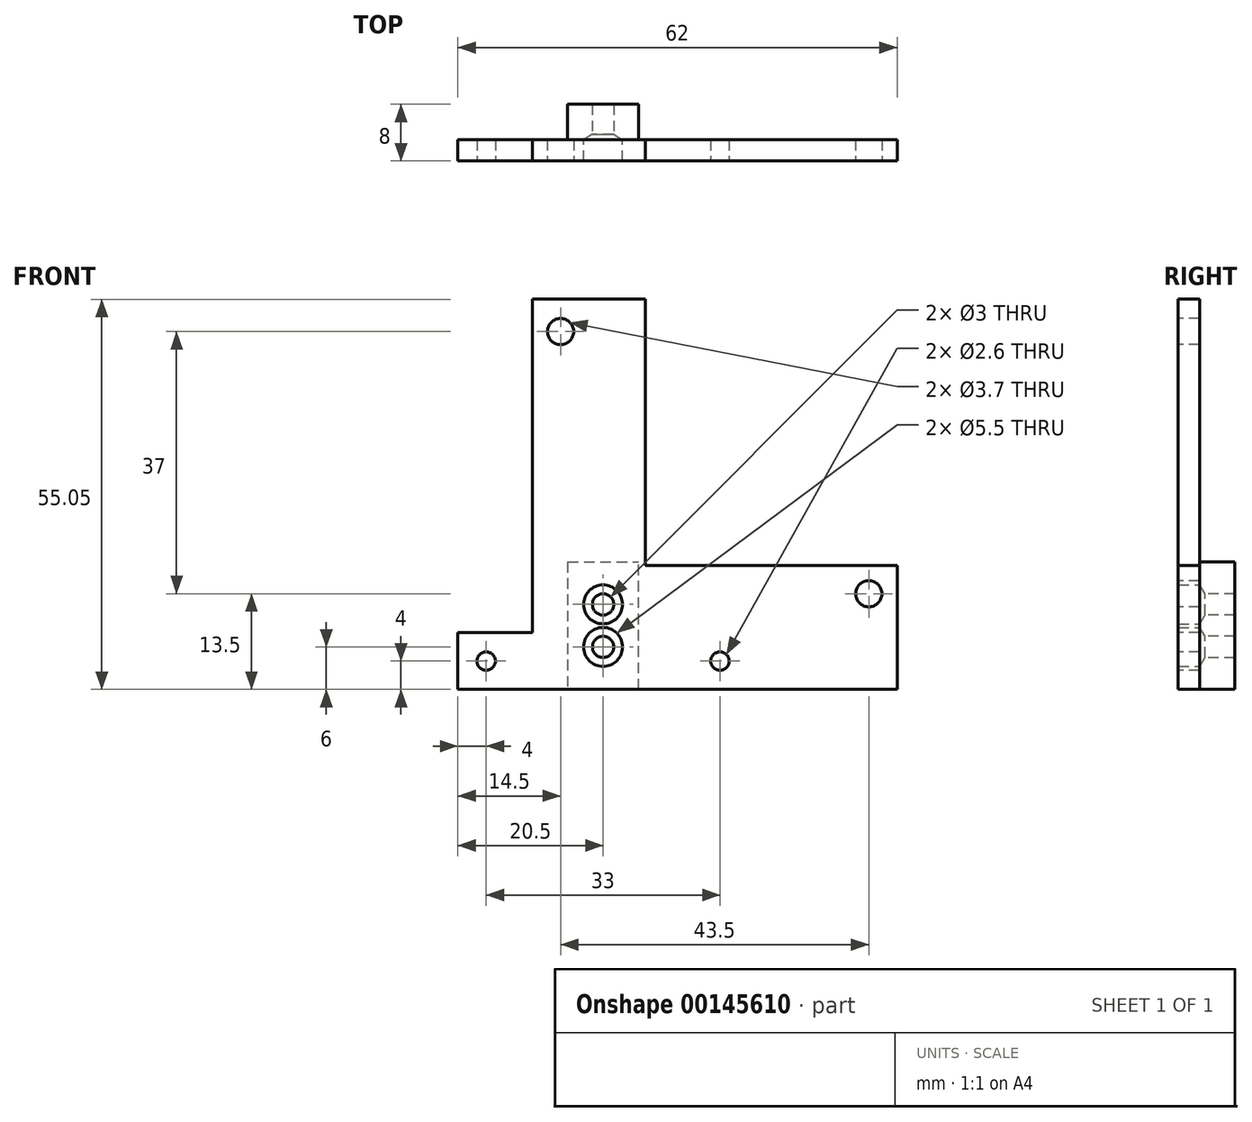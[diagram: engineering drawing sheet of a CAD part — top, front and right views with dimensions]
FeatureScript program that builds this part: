
annotation { "Feature Type Name" : "Feature", "Feature Type Description" : "" }
export const myFeature = defineFeature(function(context is Context, id is Id, definition is map)
    precondition{}
    {
        {
            var Q0;
            Q0=qCreatedBy(makeId("Front.planeOp"),FACE);
            var sketch = newSketch(context, id + "F0", { "sketchPlane" : qUnion([Q0])});
            skLineSegment(sketch, "E0", {"start": v(10, 73.44) * mm, "end": v(10, -53.24) * mm, "construction": true});
            skCircle(sketch, "E1", {"center": v(-6.5, -1) * mm, "radius": 1.3 * mm});
            skCircle(sketch, "E2", {"center": v(26.5, -1) * mm, "radius": 1.3 * mm});
            skCircle(sketch, "E3", {"center": v(4, 45.5) * mm, "radius": 1.85 * mm});
            skCircle(sketch, "E4", {"center": v(47.5, 8.5) * mm, "radius": 1.85 * mm});
            skLineSegment(sketch, "E5", {"start": v(-10.5, 3) * mm, "end": v(-10.5, -5) * mm});
            skLineSegment(sketch, "E6", {"start": v(-10.5, -5) * mm, "end": v(51.5, -5) * mm});
            skLineSegment(sketch, "E7", {"start": v(51.5, -5) * mm, "end": v(51.5, 12.5) * mm});
            skLineSegment(sketch, "E8", {"start": v(51.5, 12.5) * mm, "end": v(16, 12.5) * mm});
            skLineSegment(sketch, "E9", {"start": v(16, 12.5) * mm, "end": v(16, 50.05) * mm});
            skLineSegment(sketch, "E10", {"start": v(16, 50.05) * mm, "end": v(0, 50.05) * mm});
            skLineSegment(sketch, "E11", {"start": v(0, 50.05) * mm, "end": v(0, 3) * mm});
            skLineSegment(sketch, "E12", {"start": v(0, 3) * mm, "end": v(-10.5, 3) * mm});
            skCircle(sketch, "E13", {"center": v(10, 7) * mm, "radius": 1.5 * mm});
            skCircle(sketch, "E14", {"center": v(10, 1) * mm, "radius": 1.5 * mm});
            skLineSegment(sketch, "E15.right", {"start": v(15, -5) * mm, "end": v(15, 13) * mm});
            skLineSegment(sketch, "E16", {"start": v(5, 13) * mm, "end": v(5, -5) * mm});
            skLineSegment(sketch, "E17", {"start": v(5, 13) * mm, "end": v(15, 13) * mm});
            skSolve(sketch);
        }
        {
            var Q0;
            Q0=qSketchRegion(id+"F0",true);
            extrude(context, id + "F1", {"entities" : qUnion([Q0]), "oppositeDirection" : true, "depth" : 3 * mm, "offsetDistance" : 25 * mm});
        }
        {
            var Q0;
            Q0=makeQuery(id+"F0.imprint","IMPRINT",FACE,{"disambiguationData":[TD([[makeQuery(id+"F0.imprint","IMPRINT",EDGE,{"derivedFrom":sQuery(id+"F0.wireOp",EDGE,"E13")}),-1.0]])]});
            extrude(context, id + "F2", {"entities" : qUnion([Q0]), "operationType" : NewBodyOperationType.ADD, "oppositeDirection" : true, "depth" : 8 * mm, "offsetDistance" : 25 * mm});
        }
        {
            var Q0;
            Q0=sQuery(id+"F0.wireOp",VERTEX,"E13.center");
            var Q1;
            Q1=sQuery(id+"F0.wireOp",VERTEX,"E14.center");
            var Q2;
            Q2=makeQuery(id+"F1.opExtrude","SWEPT_BODY",BODY,{"disambiguationData":[OSD([sQuery(id+"F0.wireOp",EDGE,"E1"),sQuery(id+"F0.wireOp",EDGE,"E2"),sQuery(id+"F0.wireOp",EDGE,"E3"),sQuery(id+"F0.wireOp",EDGE,"E4"),sQuery(id+"F0.wireOp",EDGE,"LTR5Ljhv-Eu8H-ERVJ-RBGi-5GrPvZuBQSdN"),sQuery(id+"F0.wireOp",EDGE,"KoNkH6y4-ZAxL-zaCC-6vV5-txevZE0P7taB"),sQuery(id+"F0.wireOp",EDGE,"3dQlxLyk-7jtG-Ct37-r4GP-0ixBwlLNyUi0"),sQuery(id+"F0.wireOp",EDGE,"H3lf0Hv1-sSIg-UiyV-rOKO-qJLkbeJNSC4m"),sQuery(id+"F0.wireOp",EDGE,"gS85fHuh-e3na-eI1G-zhm8-VCtowNqxd4xq"),sQuery(id+"F0.wireOp",EDGE,"D0Ng3LRb-so7R-YxlR-H6ka-L2ml7fYsDFut"),sQuery(id+"F0.wireOp",EDGE,"QT1inQir-GTmR-n3ot-THxN-ZQq2sqMQ91lZ"),sQuery(id+"F0.wireOp",EDGE,"rj65UwG1-iAIk-RhY9-SyVZ-Hv82mRuWcSfV"),sQuery(id+"F0.wireOp",EDGE,"K5cZkbua-shdL-yTTr-0PsO-daTVBTCjA4YU"),sQuery(id+"F0.wireOp",EDGE,"vmWiRf7P-kd8g-lgdg-2NPn-rd3Ge1qaOaTf"),sQuery(id+"F0.wireOp",EDGE,"vCQZ20dp-zfKI-MM0t-WmvQ-ZL5dYqWUvWY3"),sQuery(id+"F0.wireOp",EDGE,"n316J1DL-DCGi-Badq-r771-MAIbQZo2Y9bQ")])]});
            hole(context, id + "F3", {"style" : HoleStyle.SIMPLE, "endStyle" : HoleEndStyle.BLIND, "holeDiameter" : 5.5 * mm, "holeDepth" : 3 * mm, "tappedDepth" : 12 * mm, "tapClearance" : 3, "locations" : qUnion([Q0, Q1]), "scope" : qUnion([Q2]), "majorDiameter" : 5 * mm});
        }
    });
